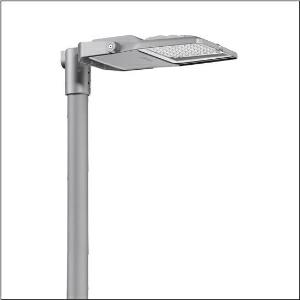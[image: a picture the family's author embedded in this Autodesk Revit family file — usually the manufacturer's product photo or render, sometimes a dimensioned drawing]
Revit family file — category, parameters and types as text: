
# Revit family: floodlight_fl_21_mini___pl43_5xa7775c2a3a_cdc0
name_source: partatom
category: Lighting Fixtures
units: mm (PartAtom-declared; Revit-internal decimal feet)

## family parameters
Cut with Voids When Loaded = No
Host = Face
Light Source = No
Part Type = Normal
Room Calculation Point = No
Round Connector Dimension = Use Diameter
Shared = No

## types (1)
- --- (1 x LED, 12500 lm, 89 W, 3000K)
    Apparent Load = 89 VA
    CIE Flux Codes = 27 78 99 100 100
    Color Rendering = 70
    Color Temperature = 3000K
    Default Elevation = 1800 mm
    Description = Floodlight FL 21 mini, floodlight, primary light control with lens, of PMMA, primary optical cover: protective disc, of toughened safety glass, transparent, light distribution: PL43, light emission: direct distribution, installation type: surface-mounted, LED, High Power LED, rated luminous flux: 12.500lm, luminous efficacy: 140lm/W, light colour: 730, colour temperature: 3000K, control: flexible luminous flux parameterisation, time-dependent luminous flux control, constant luminous flux control, overheat protection, presetting dimming logarithmic, with terminal, 6-pole, mains connection: 220..240V, AC, 50/60Hz, start of lifetime: 89W, end of service life: 94W, reduction: 43W, luminaire housing, of diecast aluminium, powder-coated, Siteco® metallic grey (DB 702S), corrosivity category C5 mid according to DIN EN ISO 12944, sealing non-destructively replaceable, please order mast flange separately, mast bracket, of steel, galvanised, powder-coated, Siteco® metallic grey (DB 702S), Smart Interface above, protection rating (complete): IP66, insulation class (complete): insulation class II (safety insulation), certification: CE, ENEC, VDE, protection symbol: D, impact resistance: IK08, permissible operating ambient temperature: -40..+40°C, permissible operating ambient temperature for outdoor applications: -40..+50°C, standard: DIN EN 12944, LABS conformity tested according to VDMA 24364:2018-05, packaging unit: 1 piece

Light Distribution: PL43
    Height = 70 mm
    Lamp = 1 x LED
    Lamp Light Flux = 12500 lm
    Lamp Power = 89 W
    Lamp count = 1
    Length = 485 mm
    Luminous efficacy = 140 lm/W
    Manufacturer = Siteco
    ModVariant = No
    Model = 5XA7775C2A3A
    Number of Poles = 1
    OnlyDefault = Yes
    Power Factor = 1
    Product Name = Floodlight FL 21 mini | PL43
    Product group = floodlight | pylon annexe
    ProductGroupID = 6200
    Protection Class = Protection class II
    Protection Degree = IP 66
    RLX_Detail_Level = 1
    RLX_Emergency_Light_Flux = 0 lm
    RLX_Emergency_Type = 0
    RLX_Emergency_Type_DB = No
    RlxData = <blob elided: 100785 chars, md5=956cdb25>
    Socket = socket
    Standby Power = 0 W
    System Light Flux = 12500 lm
    System Power = 89 W
    Type Comments = factory setting: luminous flux: 100 % | dim-lin: 254 | 456 mA
    Type Image = l_1007125.jpg
    URL = http://relux.com
    VarID = @adj_093427
    Voltage = 0 V
    Weight = 0.00 kg
    Width = 337 mm

## geometry (parser evidence)
native form markers: Blend x4, Sweep x13
no freeform markers — native parametric forms only
